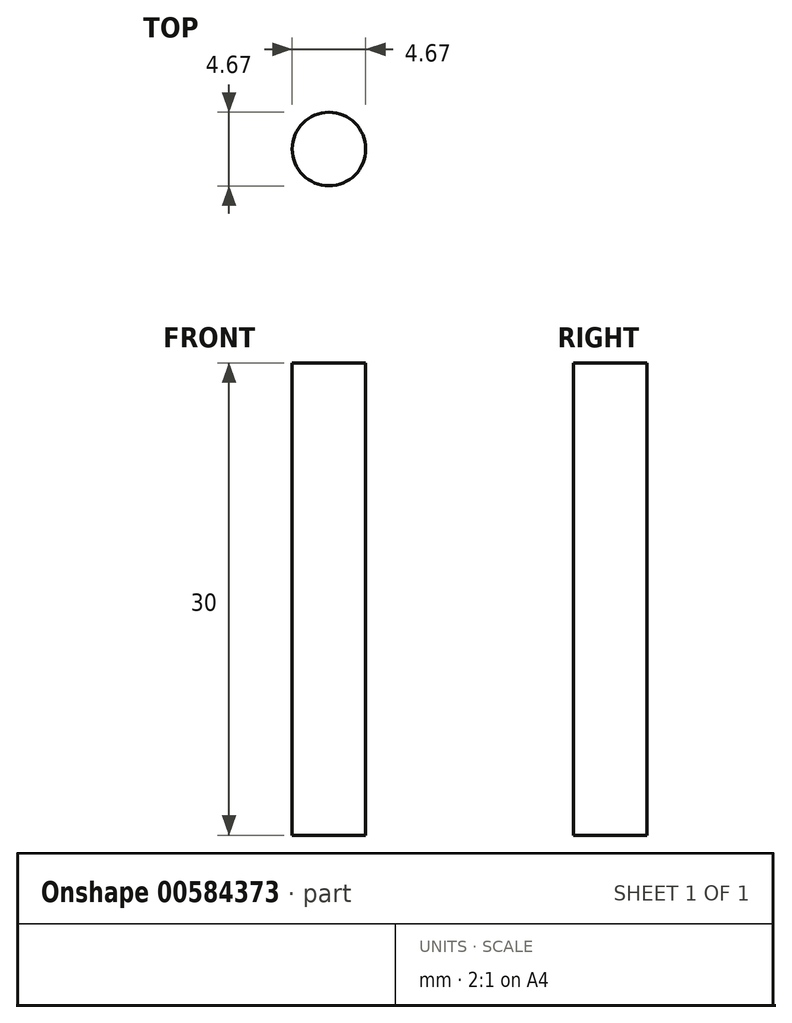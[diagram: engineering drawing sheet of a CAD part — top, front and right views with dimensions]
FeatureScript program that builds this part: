
annotation { "Feature Type Name" : "Feature", "Feature Type Description" : "" }
export const myFeature = defineFeature(function(context is Context, id is Id, definition is map)
    precondition{}
    {
        {
            var Q0;
            Q0=qCreatedBy(makeId("Top.planeOp"),FACE);
            var sketch = newSketch(context, id + "F0", { "sketchPlane" : qUnion([Q0])});
            skCircle(sketch, "E0", {"center": v(5.82, -16.21) * mm, "radius": 2.34 * mm});
            skSolve(sketch);
        }
        {
            var Q0;
            Q0 = qSketchRegion(id + "F0", true);
            extrude(context, id + "F1", {"entities" : qUnion([Q0]), "depth" : 30 * mm, "offsetDistance" : 25 * mm});
        }
    });
